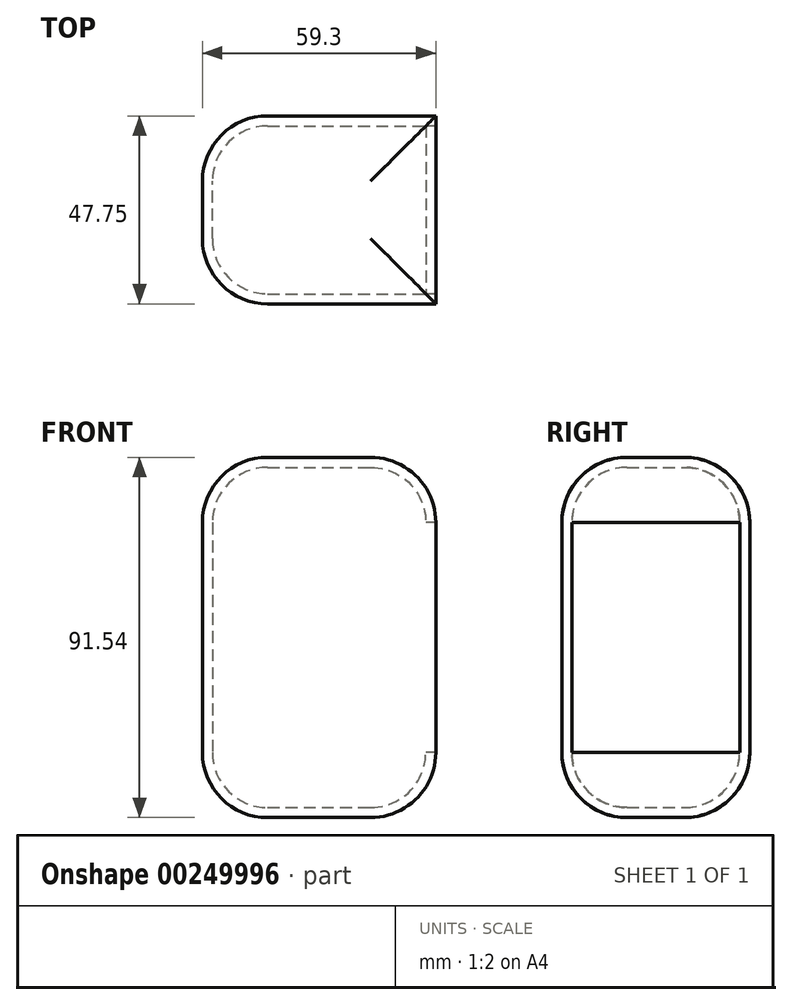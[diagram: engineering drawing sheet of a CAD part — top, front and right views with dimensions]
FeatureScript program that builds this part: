
annotation { "Feature Type Name" : "Feature", "Feature Type Description" : "" }
export const myFeature = defineFeature(function(context is Context, id is Id, definition is map)
    precondition{}
    {
        {
            var Q0;
            Q0=qCreatedBy(makeId("Front.planeOp"),FACE);
            var sketch = newSketch(context, id + "F0", { "sketchPlane" : qUnion([Q0])});
            skLineSegment(sketch, "E0.bottom", {"start": v(-30.36, 38.6) * mm, "end": v(28.94, 38.6) * mm});
            skLineSegment(sketch, "E0.top", {"start": v(-30.36, -52.95) * mm, "end": v(28.94, -52.95) * mm});
            skLineSegment(sketch, "E0.left", {"start": v(-30.36, 38.6) * mm, "end": v(-30.36, -52.95) * mm});
            skLineSegment(sketch, "E0.right", {"start": v(28.94, 38.6) * mm, "end": v(28.94, -52.95) * mm});
            skSolve(sketch);
        }
        {
            var Q0;
            Q0=makeQuery(id+"F0.imprint","IMPRINT",FACE,{"disambiguationData":[TD([[makeQuery(id+"F0.imprint","IMPRINT",EDGE,{"derivedFrom":sQuery(id+"F0.wireOp",EDGE,"E0.bottom")}),-1.0]])]});
            extrude(context, id + "F1", {"entities" : qUnion([Q0]), "depth" : 47.75 * mm});
        }
        {
            var Q0;
            Q0=makeQuery(id+"F1.opExtrude","SWEPT_FACE",FACE,{"disambiguationData":[OSD([sQuery(id+"F0.wireOp",EDGE,"E0.left")])]});
            var Q1;
            Q1=makeQuery(id+"F1.opExtrude","SWEPT_FACE",FACE,{"disambiguationData":[OSD([sQuery(id+"F0.wireOp",EDGE,"E0.top")])]});
            var Q2;
            Q2=makeQuery(id+"F1.opExtrude","SWEPT_FACE",FACE,{"disambiguationData":[OSD([sQuery(id+"F0.wireOp",EDGE,"E0.bottom")])]});
            fillet(context, id + "F2", {"entities" : qUnion([Q0, Q1, Q2]), "radius" : 16.56 * mm, "tangentPropagation" : true, "allowEdgeOverflow" : false});
        }
        {
            var Q0;
            Q0=makeQuery(id+"F1.opExtrude","SWEPT_FACE",FACE,{"disambiguationData":[OSD([sQuery(id+"F0.wireOp",EDGE,"E0.right")])]});
            shell(context, id + "F3", {"entities" : qUnion([Q0]), "thickness" : 2.54 * mm});
        }
    });
